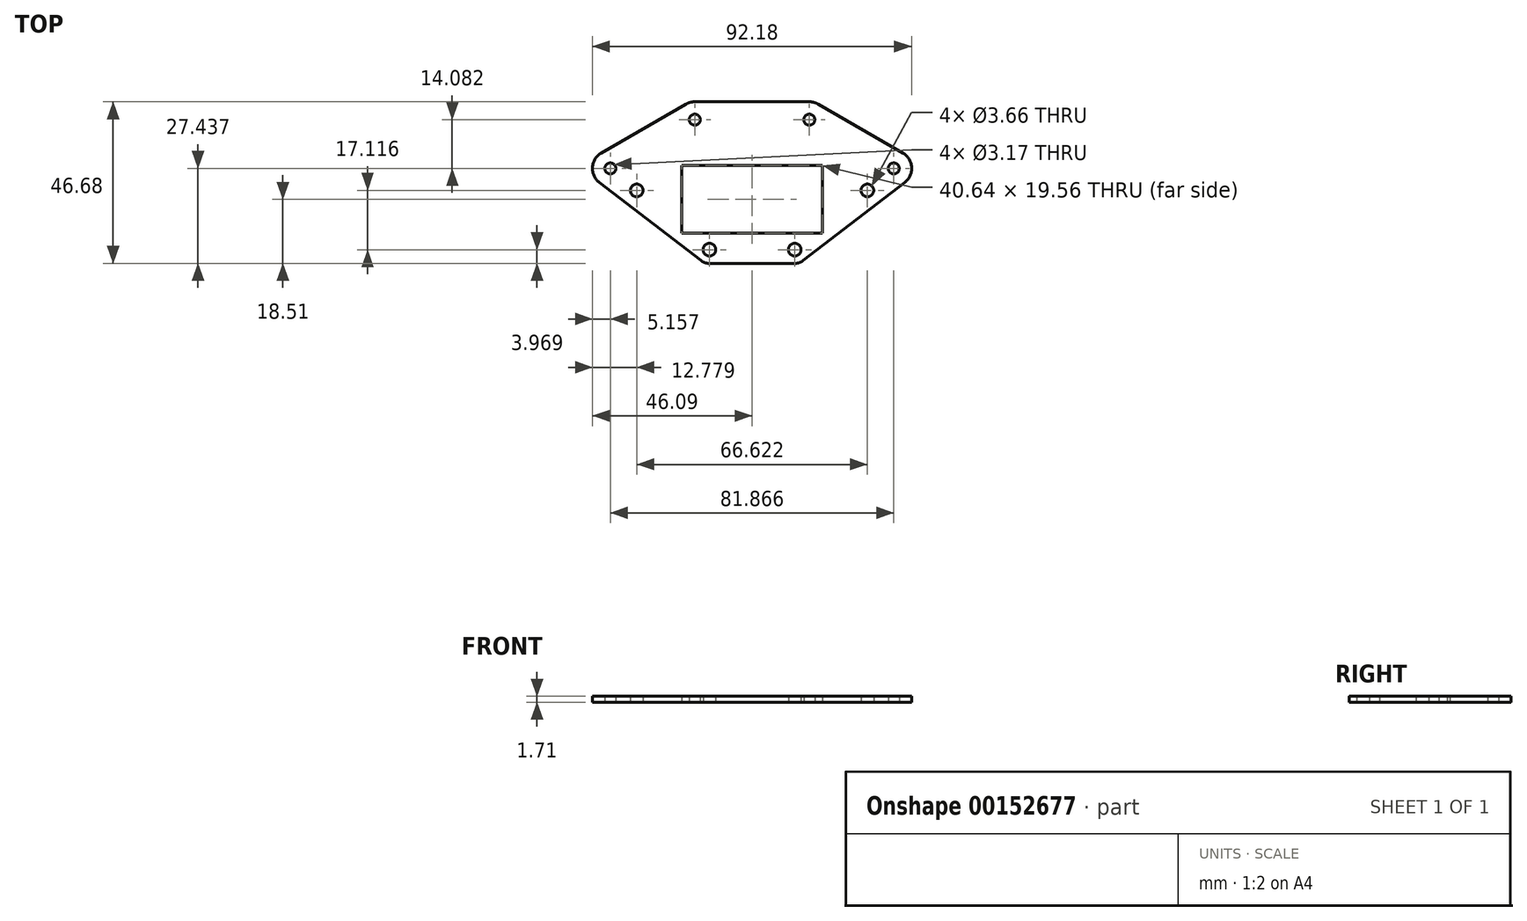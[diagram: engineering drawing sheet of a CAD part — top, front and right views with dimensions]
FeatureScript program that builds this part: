
annotation { "Feature Type Name" : "Feature", "Feature Type Description" : "" }
export const myFeature = defineFeature(function(context is Context, id is Id, definition is map)
    precondition{}
    {
        {
            var Q0;
            Q0=qCreatedBy(makeId("Top.planeOp"),FACE);
            var sketch = newSketch(context, id + "F0", { "sketchPlane" : qUnion([Q0])});
            skLineSegment(sketch, "E0.bottom", {"start": v(20.32, -1.02) * mm, "end": v(23.75, -1.02) * mm, "construction": true});
            skLineSegment(sketch, "E0.top", {"start": v(20.32, 1.02) * mm, "end": v(23.75, 1.02) * mm, "construction": true});
            skLineSegment(sketch, "E0.left", {"start": v(20.32, -1.02) * mm, "end": v(20.32, 1.02) * mm});
            skLineSegment(sketch, "E0.right", {"start": v(23.75, -1.02) * mm, "end": v(23.75, 1.02) * mm, "construction": true});
            skLineSegment(sketch, "E1.top", {"start": v(20.32, -9.78) * mm, "end": v(-20.32, -9.78) * mm});
            skLineSegment(sketch, "E1.left", {"start": v(20.32, -1.02) * mm, "end": v(20.32, -9.78) * mm});
            skLineSegment(sketch, "E1.right", {"start": v(-20.32, -1.02) * mm, "end": v(-20.32, -9.78) * mm});
            skLineSegment(sketch, "E2.bottom", {"start": v(-20.32, -1.02) * mm, "end": v(-23.75, -1.02) * mm, "construction": true});
            skLineSegment(sketch, "E2.top", {"start": v(-20.32, 1.02) * mm, "end": v(-23.75, 1.02) * mm, "construction": true});
            skLineSegment(sketch, "E2.left", {"start": v(-20.32, -1.02) * mm, "end": v(-20.32, 1.02) * mm});
            skLineSegment(sketch, "E2.right", {"start": v(-23.75, -1.02) * mm, "end": v(-23.75, 1.02) * mm, "construction": true});
            skLineSegment(sketch, "E3.top", {"start": v(20.32, 9.78) * mm, "end": v(-20.32, 9.78) * mm});
            skLineSegment(sketch, "E3.left", {"start": v(20.32, 1.02) * mm, "end": v(20.32, 9.78) * mm});
            skLineSegment(sketch, "E3.right", {"start": v(-20.32, 1.02) * mm, "end": v(-20.32, 9.78) * mm});
            skArc(sketch, "E4", {"start": v(23.75, -1.02) * mm, "mid": v(24.77, 0) * mm, "end": v(23.75, 1.02) * mm, "construction": true});
            skArc(sketch, "E5", {"start": v(-23.75, 1.02) * mm, "mid": v(-24.76, 0) * mm, "end": v(-23.75, -1.02) * mm, "construction": true});
            skLineSegment(sketch, "E6", {"start": v(0, -9.78) * mm, "end": v(0, 9.78) * mm, "construction": true});
            skLineSegment(sketch, "E7.bottom", {"start": v(24.9, 4.89) * mm, "end": v(-24.9, 4.89) * mm, "construction": true});
            skLineSegment(sketch, "E7.top", {"start": v(24.9, -4.89) * mm, "end": v(-24.9, -4.89) * mm, "construction": true});
            skLineSegment(sketch, "E7.left", {"start": v(24.9, 4.89) * mm, "end": v(24.9, -4.89) * mm, "construction": true});
            skLineSegment(sketch, "E7.right", {"start": v(-24.9, 4.89) * mm, "end": v(-24.9, -4.89) * mm, "construction": true});
            skPoint(sketch, "E7.middle", {"position": v(0, 0) * mm});
            skCircle(sketch, "E8", {"center": v(-24.9, 4.89) * mm, "radius": 1.73 * mm, "construction": true});
            skCircle(sketch, "E9", {"center": v(-24.9, -4.89) * mm, "radius": 1.73 * mm, "construction": true});
            skCircle(sketch, "E10", {"center": v(24.9, -4.89) * mm, "radius": 1.73 * mm, "construction": true});
            skCircle(sketch, "E11", {"center": v(24.9, 4.89) * mm, "radius": 1.73 * mm, "construction": true});
            skLineSegment(sketch, "E12", {"start": v(-20.32, 0) * mm, "end": v(-10.9, 0) * mm, "construction": true});
            skLineSegment(sketch, "E13", {"start": v(0, 9.78) * mm, "end": v(0, 23) * mm, "construction": true});
            skLineSegment(sketch, "E14", {"start": v(-16.54, 23) * mm, "end": v(16.54, 23) * mm, "construction": true});
            skLineSegment(sketch, "E15", {"start": v(16.54, 23) * mm, "end": v(40.93, 8.93) * mm, "construction": true});
            skLineSegment(sketch, "E16", {"start": v(-16.54, 23) * mm, "end": v(-40.93, 8.93) * mm, "construction": true});
            skCircle(sketch, "E17", {"center": v(40.93, 8.93) * mm, "radius": 1.59 * mm});
            skCircle(sketch, "E18", {"center": v(16.54, 23) * mm, "radius": 1.59 * mm});
            skCircle(sketch, "E19", {"center": v(-16.54, 23) * mm, "radius": 1.59 * mm});
            skCircle(sketch, "E20", {"center": v(-40.93, 8.93) * mm, "radius": 1.59 * mm});
            skLineSegment(sketch, "E21", {"start": v(-16.54, 23) * mm, "end": v(-10.9, 0) * mm, "construction": true});
            skLineSegment(sketch, "E22", {"start": v(0, 23) * mm, "end": v(0, 28.17) * mm, "construction": true});
            skLineSegment(sketch, "E23", {"start": v(40.93, 8.93) * mm, "end": v(0, 8.93) * mm, "construction": true});
            skLineSegment(sketch, "E24", {"start": v(0, 8.93) * mm, "end": v(-40.93, 8.93) * mm, "construction": true});
            skLineSegment(sketch, "E25", {"start": v(-16.54, 28.17) * mm, "end": v(16.54, 28.17) * mm});
            skArc(sketch, "E26", {"start": v(44.07, 4.83) * mm, "mid": v(46.08, 9.26) * mm, "end": v(43.51, 13.4) * mm});
            skArc(sketch, "E27", {"start": v(19.12, 27.48) * mm, "mid": v(17.88, 28) * mm, "end": v(16.54, 28.17) * mm});
            skArc(sketch, "E28", {"start": v(-16.54, 28.17) * mm, "mid": v(-17.88, 28) * mm, "end": v(-19.12, 27.48) * mm});
            skArc(sketch, "E29", {"start": v(-43.51, 13.4) * mm, "mid": v(-46.08, 9.26) * mm, "end": v(-44.07, 4.83) * mm});
            skLineSegment(sketch, "E30", {"start": v(19.12, 27.48) * mm, "end": v(43.51, 13.4) * mm});
            skLineSegment(sketch, "E31", {"start": v(-19.12, 27.48) * mm, "end": v(-43.51, 13.4) * mm});
            skLineSegment(sketch, "E32", {"start": v(-44.07, 4.83) * mm, "end": v(-14.74, -17.69) * mm});
            skLineSegment(sketch, "E33", {"start": v(44.07, 4.83) * mm, "end": v(14.74, -17.69) * mm});
            skArc(sketch, "E34", {"start": v(-14.74, -17.69) * mm, "mid": v(-13.6, -18.3) * mm, "end": v(-12.32, -18.51) * mm});
            skArc(sketch, "E35", {"start": v(12.32, -18.51) * mm, "mid": v(13.6, -18.3) * mm, "end": v(14.74, -17.69) * mm});
            skLineSegment(sketch, "E36", {"start": v(0, -9.78) * mm, "end": v(0, -14.54) * mm, "construction": true});
            skLineSegment(sketch, "E37", {"start": v(-12.32, -14.54) * mm, "end": v(12.32, -14.54) * mm, "construction": true});
            skLineSegment(sketch, "E38", {"start": v(0, -14.54) * mm, "end": v(0, -18.51) * mm, "construction": true});
            skLineSegment(sketch, "E39", {"start": v(-12.32, -18.51) * mm, "end": v(12.32, -18.51) * mm});
            skCircle(sketch, "E40", {"center": v(-12.32, -14.54) * mm, "radius": 1.83 * mm});
            skCircle(sketch, "E41", {"center": v(12.32, -14.54) * mm, "radius": 1.83 * mm});
            skCircle(sketch, "E42", {"center": v(24.9, -4.89) * mm, "radius": 3.97 * mm, "construction": true});
            skLineSegment(sketch, "E43", {"start": v(24.9, -4.89) * mm, "end": v(33.31, 2.57) * mm, "construction": true});
            skCircle(sketch, "E44", {"center": v(33.31, 2.57) * mm, "radius": 4.76 * mm, "construction": true});
            skCircle(sketch, "E45", {"center": v(33.31, 2.57) * mm, "radius": 1.83 * mm});
            skLineSegment(sketch, "E46", {"start": v(-24.9, -4.89) * mm, "end": v(-33.31, 2.57) * mm, "construction": true});
            skCircle(sketch, "E47", {"center": v(-33.31, 2.57) * mm, "radius": 4.76 * mm, "construction": true});
            skCircle(sketch, "E48", {"center": v(-33.31, 2.57) * mm, "radius": 1.83 * mm});
            skCircle(sketch, "E49", {"center": v(24.9, 4.89) * mm, "radius": 3.97 * mm, "construction": true});
            skArc(sketch, "E50", {"start": v(43.51, 13.4) * mm, "mid": v(35.78, 8.59) * mm, "end": v(44.07, 4.83) * mm, "construction": true});
            skSolve(sketch);
        }
        {
            var Q0;
            Q0=qSketchRegion(id+"F0",true);
            extrude(context, id + "F1", {"entities" : qUnion([Q0]), "depth" : 1.7 * mm});
        }
    });
